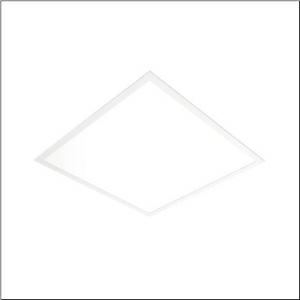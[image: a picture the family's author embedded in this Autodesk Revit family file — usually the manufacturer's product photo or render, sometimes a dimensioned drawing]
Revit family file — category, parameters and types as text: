
# Revit family: apollon_r__41_51mh12wd2422_e36b
name_source: partatom
category: Lighting Fixtures
units: mm (PartAtom-declared; Revit-internal decimal feet)

## family parameters
Cut with Voids When Loaded = No
Host = Face
Light Source = No
Part Type = Normal
Room Calculation Point = No
Round Connector Dimension = Use Diameter
Shared = No

## types (1)
- Apollon® 41 (1 x LED, 3700 lm, 35 W, 4000K)
    Apparent Load = 35 VA
    CIE Flux Codes = 63 87 97 100 100
    Color Rendering = 80
    Color Temperature = 4000K
    Default Elevation = 1800 mm
    Description = Apollon® 41, office luminaire, primary optical cover: prismatic diffuser, of PS, light emission: direct distribution, primary light characteristic: symmetric, installation type: lay-in mounting, LED, rated luminous flux: 3.700lm, luminous efficacy: 105lm/W, light colour: 840, colour temperature: 4000K, control gear: ECG DALI, with terminal, 5-pole, mains connection: 220..240V, AC, 50/60Hz, rated input power: 35W, housing, of aluminium section, traffic white (RAL 9016), module: M600, length: 595mm, width: 595mm, height: 32mm, housing upper side, of sheet steel, protection rating (complete): IP20, protection rating (lamp compartment, on room side): IP40, insulation class (complete): insulation class II (safety insulation), certification: CE, ENEC, permissible operating ambient temperature: -20..+40°C, packaging unit: 1 piece
    Height = 0 mm  [stored 0 ft]
    Lamp = 1 x LED
    Lamp Light Flux = 3700 lm
    Lamp Power = 35 W
    Lamp count = 1
    Length = 596 mm
    Luminous efficacy = 106 lm/W
    Manufacturer = Siteco
    ModVariant = No
    Model = 51MH12WD2422
    Mounting Place = Ceiling
    Mounting Type = Recessed
    Number of Poles = 1
    OnlyDefault = Yes
    Power Factor = 1
    Product Name = Apollon® 41
    Product group = office luminaire | ceiling recessed
    ProductGroupID = 400
    Protection Class = Protection class II
    Protection Degree = IP 20
    RLX_Detail_Level = 1
    RlxData = <blob elided: 14881 chars, md5=82f589ce>
    Socket = socket
    Standby Power = 0 W
    System Light Flux = 3700 lm
    System Power = 35 W
    Type Comments = Product without accessories
    Type Image = l_1003755.jpg
    URL = http://relux.com
    VarID = ---
    Voltage = 0 V
    Weight = 0.00 kg
    Width = 596 mm

note: [stored X ft] marks values corroborated as IEEE doubles in the binary element streams (Revit-internal decimal feet)

## geometry (parser evidence)
native form markers: Sweep x11
no freeform markers — native parametric forms only
